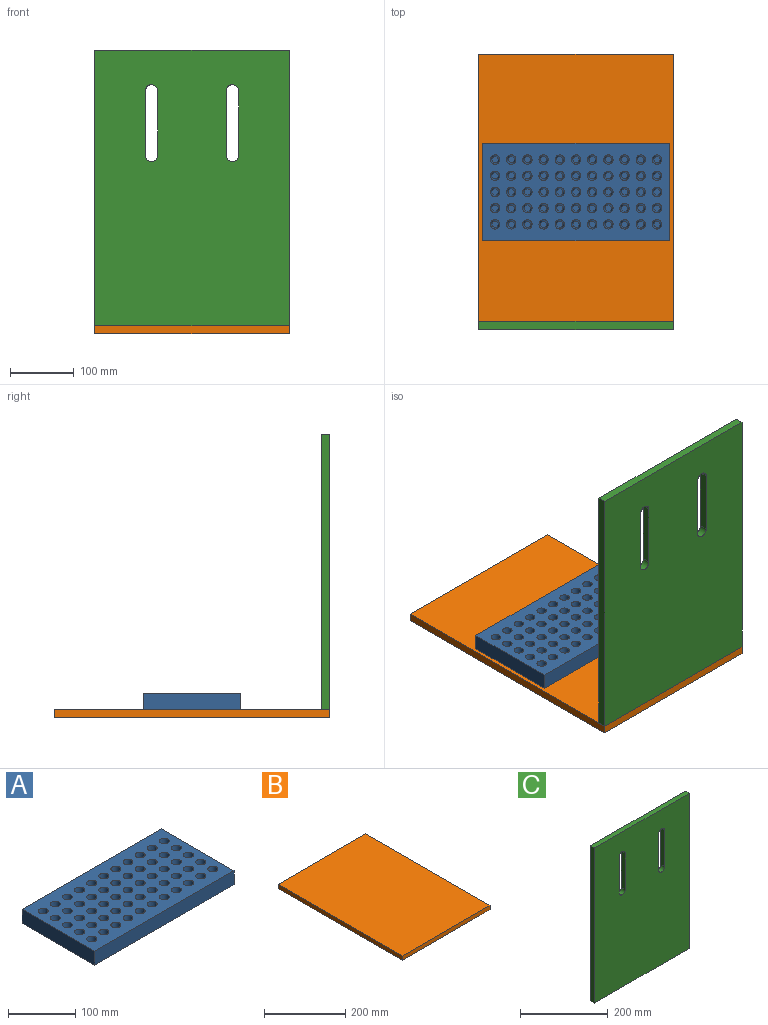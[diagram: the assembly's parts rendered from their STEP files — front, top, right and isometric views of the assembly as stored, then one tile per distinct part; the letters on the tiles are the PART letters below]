
ASSEMBLY  parts=3 mates=2
PART A: 116 faces, bbox 292.1x152.4x25.4 mm
  f0: plane 152.4x25.4mm, normal (1,0,0), area 3871mm2, adj f1,f3,f4,f5
  f1: plane 292.1x25.4mm, normal (0,1,0), area 7419.3mm2, adj f0,f2,f4,f5
  f2: plane 152.4x25.4mm, normal (-1,0,0), area 3871mm2, adj f1,f3,f4,f5
  f3: plane 292.1x25.4mm, normal (0,-1,0), area 7419.3mm2, adj f0,f2,f4,f5
  f4: plane 292.1x152.4mm, normal (0,0,1), area 35140.9mm2, adj f0,f1,f2,f3,f6,f8,f10,f12
  f5: plane 292.1x152.4mm, normal (0,0,-1), area 44516mm2, adj f0,f1,f2,f3
  f6: cone r=7.37mm half-angle=7deg, axis (0,0,1), area 747.3mm2, adj f4,f7
  f7: plane 10.05x10.05mm, normal (0,0,1), area 79.4mm2, adj f6
  f8: cone r=7.37mm half-angle=7deg, axis (0,0,1), area 747.3mm2, adj f4,f9
  f9: plane 10.05x10.05mm, normal (0,0,1), area 79.4mm2, adj f8
  f10: cone r=7.37mm half-angle=7deg, axis (0,0,1), area 747.3mm2, adj f4,f11
  f11: plane 10.05x10.05mm, normal (0,0,1), area 79.4mm2, adj f10
  f12: cone r=7.37mm half-angle=7deg, axis (0,0,1), area 747.3mm2, adj f4,f13
  f13: plane 10.05x10.05mm, normal (0,0,1), area 79.4mm2, adj f12
  f14: cone r=7.37mm half-angle=7deg, axis (0,0,1), area 747.3mm2, adj f4,f15
  f15: plane 10.05x10.05mm, normal (0,0,1), area 79.4mm2, adj f14
  f16: cone r=7.37mm half-angle=7deg, axis (0,0,1), area 747.3mm2, adj f4,f17
  f17: plane 10.05x10.05mm, normal (0,0,1), area 79.4mm2, adj f16
  f18: cone r=7.37mm half-angle=7deg, axis (0,0,1), area 747.3mm2, adj f4,f19
  f19: plane 10.05x10.05mm, normal (0,0,1), area 79.4mm2, adj f18
  f20: cone r=7.37mm half-angle=7deg, axis (0,0,1), area 747.3mm2, adj f4,f21
  f21: plane 10.05x10.05mm, normal (0,0,1), area 79.4mm2, adj f20
  f22: cone r=7.37mm half-angle=7deg, axis (0,0,1), area 747.3mm2, adj f4,f23
  f23: plane 10.05x10.05mm, normal (0,0,1), area 79.4mm2, adj f22
  f24: cone r=7.37mm half-angle=7deg, axis (0,0,1), area 747.3mm2, adj f4,f25
  f25: plane 10.05x10.05mm, normal (0,0,1), area 79.4mm2, adj f24
  f26: cone r=7.37mm half-angle=7deg, axis (0,0,1), area 747.3mm2, adj f4,f27
  f27: plane 10.05x10.05mm, normal (0,0,1), area 79.4mm2, adj f26
  f28: cone r=7.37mm half-angle=7deg, axis (0,0,1), area 747.3mm2, adj f4,f29
  f29: plane 10.05x10.05mm, normal (0,0,1), area 79.4mm2, adj f28
  f30: cone r=7.37mm half-angle=7deg, axis (0,0,1), area 747.3mm2, adj f4,f31
  f31: plane 10.05x10.05mm, normal (0,0,1), area 79.4mm2, adj f30
  f32: cone r=7.37mm half-angle=7deg, axis (0,0,1), area 747.3mm2, adj f4,f33
  f33: plane 10.05x10.05mm, normal (0,0,1), area 79.4mm2, adj f32
  f34: cone r=7.37mm half-angle=7deg, axis (0,0,1), area 747.3mm2, adj f4,f35
  f35: plane 10.05x10.05mm, normal (0,0,1), area 79.4mm2, adj f34
  f36: cone r=7.37mm half-angle=7deg, axis (0,0,1), area 747.3mm2, adj f4,f37
  f37: plane 10.05x10.05mm, normal (0,0,1), area 79.4mm2, adj f36
  f38: cone r=7.37mm half-angle=7deg, axis (0,0,1), area 747.3mm2, adj f4,f39
  f39: plane 10.05x10.05mm, normal (0,0,1), area 79.4mm2, adj f38
  f40: cone r=7.37mm half-angle=7deg, axis (0,0,1), area 747.3mm2, adj f4,f41
  f41: plane 10.05x10.05mm, normal (0,0,1), area 79.4mm2, adj f40
  f42: cone r=7.37mm half-angle=7deg, axis (0,0,1), area 747.3mm2, adj f4,f43
  f43: plane 10.05x10.05mm, normal (0,0,1), area 79.4mm2, adj f42
  f44: cone r=7.37mm half-angle=7deg, axis (0,0,1), area 747.3mm2, adj f4,f45
  f45: plane 10.05x10.05mm, normal (0,0,1), area 79.4mm2, adj f44
  f46: cone r=7.37mm half-angle=7deg, axis (0,0,1), area 747.3mm2, adj f4,f47
  f47: plane 10.05x10.05mm, normal (0,0,1), area 79.4mm2, adj f46
  f48: cone r=7.37mm half-angle=7deg, axis (0,0,1), area 747.3mm2, adj f4,f49
  f49: plane 10.05x10.05mm, normal (0,0,1), area 79.4mm2, adj f48
  f50: cone r=7.37mm half-angle=7deg, axis (0,0,1), area 747.3mm2, adj f4,f51
  f51: plane 10.05x10.05mm, normal (0,0,1), area 79.4mm2, adj f50
  f52: cone r=7.37mm half-angle=7deg, axis (0,0,1), area 747.3mm2, adj f4,f53
  f53: plane 10.05x10.05mm, normal (0,0,1), area 79.4mm2, adj f52
  f54: cone r=7.37mm half-angle=7deg, axis (0,0,1), area 747.3mm2, adj f4,f55
  f55: plane 10.05x10.05mm, normal (0,0,1), area 79.4mm2, adj f54
  f56: cone r=7.37mm half-angle=7deg, axis (0,0,1), area 747.3mm2, adj f4,f57
  f57: plane 10.05x10.05mm, normal (0,0,1), area 79.4mm2, adj f56
  f58: cone r=7.37mm half-angle=7deg, axis (0,0,1), area 747.3mm2, adj f4,f59
  f59: plane 10.05x10.05mm, normal (0,0,1), area 79.4mm2, adj f58
  f60: cone r=7.37mm half-angle=7deg, axis (0,0,1), area 747.3mm2, adj f4,f61
  f61: plane 10.05x10.05mm, normal (0,0,1), area 79.4mm2, adj f60
  f62: cone r=7.37mm half-angle=7deg, axis (0,0,1), area 747.3mm2, adj f4,f63
  f63: plane 10.05x10.05mm, normal (0,0,1), area 79.4mm2, adj f62
  f64: cone r=7.37mm half-angle=7deg, axis (0,0,1), area 747.3mm2, adj f4,f65
  f65: plane 10.05x10.05mm, normal (0,0,1), area 79.4mm2, adj f64
  f66: cone r=7.37mm half-angle=7deg, axis (0,0,1), area 747.3mm2, adj f4,f67
  f67: plane 10.05x10.05mm, normal (0,0,1), area 79.4mm2, adj f66
  f68: cone r=7.37mm half-angle=7deg, axis (0,0,1), area 747.3mm2, adj f4,f69
  f69: plane 10.05x10.05mm, normal (0,0,1), area 79.4mm2, adj f68
  f70: cone r=7.37mm half-angle=7deg, axis (0,0,1), area 747.3mm2, adj f4,f71
  f71: plane 10.05x10.05mm, normal (0,0,1), area 79.4mm2, adj f70
  f72: cone r=7.37mm half-angle=7deg, axis (0,0,1), area 747.3mm2, adj f4,f73
  f73: plane 10.05x10.05mm, normal (0,0,1), area 79.4mm2, adj f72
  f74: cone r=7.37mm half-angle=7deg, axis (0,0,1), area 747.3mm2, adj f4,f75
  f75: plane 10.05x10.05mm, normal (0,0,1), area 79.4mm2, adj f74
  f76: cone r=7.37mm half-angle=7deg, axis (0,0,1), area 747.3mm2, adj f4,f77
  f77: plane 10.05x10.05mm, normal (0,0,1), area 79.4mm2, adj f76
  f78: cone r=7.37mm half-angle=7deg, axis (0,0,1), area 747.3mm2, adj f4,f79
  f79: plane 10.05x10.05mm, normal (0,0,1), area 79.4mm2, adj f78
  f80: cone r=7.37mm half-angle=7deg, axis (0,0,1), area 747.3mm2, adj f4,f81
  f81: plane 10.05x10.05mm, normal (0,0,1), area 79.4mm2, adj f80
  f82: cone r=7.37mm half-angle=7deg, axis (0,0,1), area 747.3mm2, adj f4,f83
  f83: plane 10.05x10.05mm, normal (0,0,1), area 79.4mm2, adj f82
  f84: cone r=7.37mm half-angle=7deg, axis (0,0,1), area 747.3mm2, adj f4,f85
  f85: plane 10.05x10.05mm, normal (0,0,1), area 79.4mm2, adj f84
  f86: cone r=7.37mm half-angle=7deg, axis (0,0,1), area 747.3mm2, adj f4,f87
  f87: plane 10.05x10.05mm, normal (0,0,1), area 79.4mm2, adj f86
  f88: cone r=7.37mm half-angle=7deg, axis (0,0,1), area 747.3mm2, adj f4,f89
  f89: plane 10.05x10.05mm, normal (0,0,1), area 79.4mm2, adj f88
  f90: cone r=7.37mm half-angle=7deg, axis (0,0,1), area 747.3mm2, adj f4,f91
  f91: plane 10.05x10.05mm, normal (0,0,1), area 79.4mm2, adj f90
  f92: cone r=7.37mm half-angle=7deg, axis (0,0,1), area 747.3mm2, adj f4,f93
  f93: plane 10.05x10.05mm, normal (0,0,1), area 79.4mm2, adj f92
  f94: cone r=7.37mm half-angle=7deg, axis (0,0,1), area 747.3mm2, adj f4,f95
  f95: plane 10.05x10.05mm, normal (0,0,1), area 79.4mm2, adj f94
  f96: cone r=7.37mm half-angle=7deg, axis (0,0,1), area 747.3mm2, adj f4,f97
  f97: plane 10.05x10.05mm, normal (0,0,1), area 79.4mm2, adj f96
  f98: cone r=7.37mm half-angle=7deg, axis (0,0,1), area 747.3mm2, adj f4,f99
  f99: plane 10.05x10.05mm, normal (0,0,1), area 79.4mm2, adj f98
  f100: cone r=7.37mm half-angle=7deg, axis (0,0,1), area 747.3mm2, adj f4,f101
  f101: plane 10.05x10.05mm, normal (0,0,1), area 79.4mm2, adj f100
  f102: cone r=7.37mm half-angle=7deg, axis (0,0,1), area 747.3mm2, adj f4,f103
  f103: plane 10.05x10.05mm, normal (0,0,1), area 79.4mm2, adj f102
  f104: cone r=7.37mm half-angle=7deg, axis (0,0,1), area 747.3mm2, adj f4,f105
  f105: plane 10.05x10.05mm, normal (0,0,1), area 79.4mm2, adj f104
  f106: cone r=7.37mm half-angle=7deg, axis (0,0,1), area 747.3mm2, adj f4,f107
  f107: plane 10.05x10.05mm, normal (0,0,1), area 79.4mm2, adj f106
  f108: cone r=7.37mm half-angle=7deg, axis (0,0,1), area 747.3mm2, adj f4,f109
  f109: plane 10.05x10.05mm, normal (0,0,1), area 79.4mm2, adj f108
  f110: cone r=7.37mm half-angle=7deg, axis (0,0,1), area 747.3mm2, adj f4,f111
  f111: plane 10.05x10.05mm, normal (0,0,1), area 79.4mm2, adj f110
  f112: cone r=7.37mm half-angle=7deg, axis (0,0,1), area 747.3mm2, adj f4,f113
  f113: plane 10.05x10.05mm, normal (0,0,1), area 79.4mm2, adj f112
  f114: cone r=7.37mm half-angle=7deg, axis (0,0,1), area 747.3mm2, adj f4,f115
  f115: plane 10.05x10.05mm, normal (0,0,1), area 79.4mm2, adj f114
PART B: 6 faces, bbox 304.8x431.8x12.7 mm
  f0: plane 431.8x12.7mm, normal (1,0,0), area 5483.9mm2, adj f1,f3,f4,f5
  f1: plane 304.8x12.7mm, normal (0,1,0), area 3871mm2, adj f0,f2,f4,f5
  f2: plane 431.8x12.7mm, normal (-1,0,0), area 5483.9mm2, adj f1,f3,f4,f5
  f3: plane 304.8x12.7mm, normal (0,-1,0), area 3871mm2, adj f0,f2,f4,f5
  f4: plane 431.8x304.8mm, normal (0,0,1), area 131612.6mm2, adj f0,f1,f2,f3
  f5: plane 431.8x304.8mm, normal (0,0,-1), area 131612.6mm2, adj f0,f1,f2,f3
PART C: 14 faces, bbox 304.8x12.7x431.8 mm
  f0: cylinder r=9.53mm len=19.03mm, axis (0,1,0), area 372.3mm2, adj f1,f11,f12,f13
  f1: plane 102.21x12.7mm, normal (-1,0,0), area 1298mm2, adj f0,f2,f12,f13
  f2: cylinder r=9.53mm len=19.05mm, axis (0,1,0), area 380.1mm2, adj f1,f11,f12,f13
  f3: cylinder r=9.53mm len=19.05mm, axis (0,1,0), area 391.3mm2, adj f4,f9,f12,f13
  f4: plane 101.6x12.7mm, normal (1,0,0), area 1290.3mm2, adj f3,f5,f12,f13
  f5: cylinder r=9.53mm len=19.04mm, axis (0,1,0), area 380mm2, adj f4,f9,f12,f13
  f6: plane 431.8x12.7mm, normal (1,0,0), area 5483.9mm2, adj f7,f10,f12,f13
  f7: plane 304.8x12.7mm, normal (0,0,1), area 3871mm2, adj f6,f8,f12,f13
  f8: plane 431.8x12.7mm, normal (-1,0,0), area 5483.9mm2, adj f7,f10,f12,f13
  f9: plane 100.72x12.7mm, normal (-1,0,0), area 1279.1mm2, adj f3,f5,f12,f13
  f10: plane 304.8x12.7mm, normal (0,0,-1), area 3871mm2, adj f6,f8,f12,f13
  f11: plane 101.6x12.7mm, normal (1,0,0), area 1290.3mm2, adj f0,f2,f12,f13
  f12: plane 431.8x304.8mm, normal (0,-1,0), area 127174.7mm2, adj f0,f1,f2,f3,f4,f5,f6,f7
  f13: plane 431.8x304.8mm, normal (0,1,0), area 127174.7mm2, adj f0,f1,f2,f3,f4,f5,f6,f7
PLACE A t=(35.14,12.46,-5.39)mm
PLACE B t=(35.14,12.46,-18.09)mm fixed
PLACE C rot(axis=(0,0,1),180deg) t=(35.14,-203.44,210.51)mm
MATE fastened C.f10 <-> B.f4  axis (0,0,-1) through (35.14,-203.44,-5.39)mm
MATE planar A.f110 <-> B.f4  axis (0,0,-1) through (35.14,12.46,-5.39)mm
